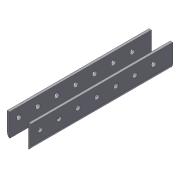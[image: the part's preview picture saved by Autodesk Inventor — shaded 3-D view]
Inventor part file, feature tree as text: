
AUTODESK INVENTOR PART (.ipt)
format: ipt  version: 2012 (Build 160160000, 160)  size: 139,264 bytes
history: native  units: in
note: dims shown in document units (in); Inventor stores cm internally (conversion verified against a paired STEP export)
features: extrude x4, sketch x4, pattern_linear x1
ambient origin geometry x8: Origin, YZ Plane, XZ Plane, XY Plane, X Axis, Y Axis, Z Axis, Center Point
bodies: Solid1 (feature_tree)
feature tree (9):
  extrude  "Extrusion1"  Depth=1.0in
  extrude  "Extrusion2"  Depth=0.125in
  pattern_linear  "Rectangular Pattern1"  Spacing1=0.5in  [1 undecoded]
  extrude  "Extrusion3"  Depth=0.5in
  extrude  "Extrusion4"  Depth=7.0in TaperAngle=0.0deg
  sketch  "Sketch1"  dims[d0=0.125in d1=1.0in]
  sketch  "Sketch2"  dims[d2=1.0in d3=0.125in]
  sketch  "Sketch3"  dims[d4=7.5in d5=0.0in]
  sketch  "Sketch4"  dims[d6=0.25in d7=0.5in d8=0.5in d9=7.0in d10=0.0in d11=2.7559in d13=1.0in d14=0.5in d15=2.0in d16=7.0in d17=0.0in d18=1.0in d19=1.125in d20=0.0in d21=0.0in d22=7.0in d23=0.0in]
note: 1 required parameter value undecoded (feature->parameter linkage not recoverable at this tier; creation-order binding heuristic only, values carry confidence <= 0.55)
